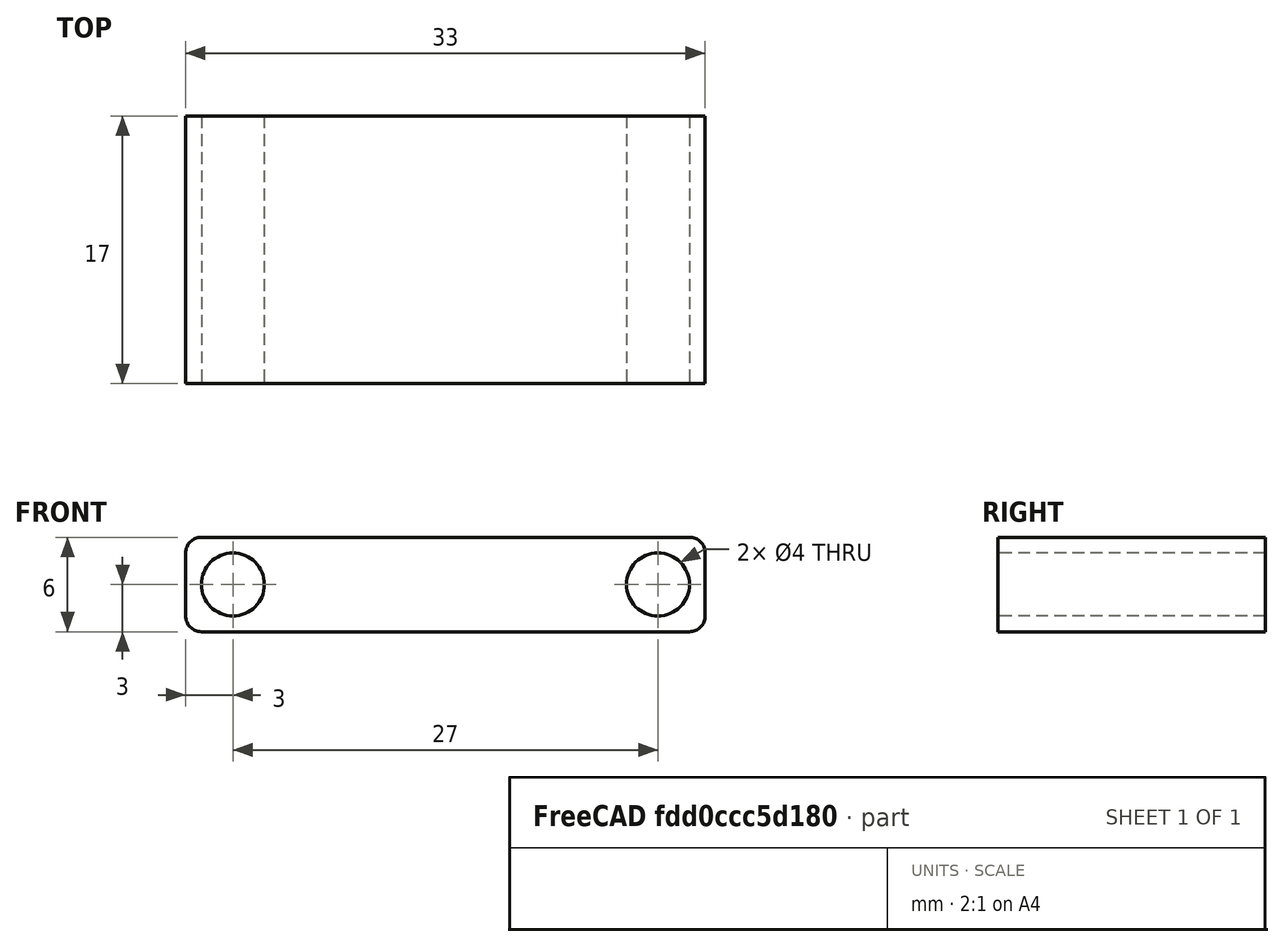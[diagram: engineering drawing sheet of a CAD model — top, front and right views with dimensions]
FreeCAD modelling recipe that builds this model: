
FCSTD DOCUMENT  (FreeCAD 0.14R3702 (Git))
Label: camera mount arm
License: CC-BY 3.0
LicenseURL: http://creativecommons.org/licenses/by/3.0/
objects: Part::Cut×4, Part::Cylinder×3, Part::Box×2, Part::Fillet×1
note: 10 computed .brp shape members not serialized (recipe doc carries the construction recipe); baked Part::Feature solids carry a one-line shape summary decoded from their .brp

FEATURE [Part::Box] Box  label="Cube"
  Height = 6
  Length = 33
  Width = 21
FEATURE [Part::Cylinder] Cylinder
  Angle = 360
  Height = 30
  Placement = pos=(3,27,3) rot=(1,0,0;1.5708rad)
  Radius = 2
FEATURE [Part::Cylinder] Cylinder001
  Angle = 360
  Height = 30
  Placement = pos=(3,27,3) rot=(1,0,0;1.5708rad)
  Radius = 2
FEATURE [Part::Cut] Cut
  Base = -> Box
  Tool = -> Cylinder
FEATURE [Part::Cut] Cut001
  Base = -> Cut
  Tool = -> Cylinder001
FEATURE [Part::Cylinder] Cylinder002
  Angle = 360
  Height = 30
  Placement = pos=(30,27,3) rot=(1,0,0;1.5708rad)
  Radius = 2
FEATURE [Part::Cut] Cut002
  Base = -> Cut001
  Tool = -> Cylinder002
FEATURE [Part::Fillet] Fillet
  Base = -> Cut002
  Edges = 4 edges r=1: [Edge2,Edge4,Edge11,Edge16]
FEATURE [Part::Box] Box001  label="Cube001"
  Height = 10
  Length = 50
  Width = 4
FEATURE [Part::Cut] Cut003
  Base = -> Fillet
  Tool = -> Box001
